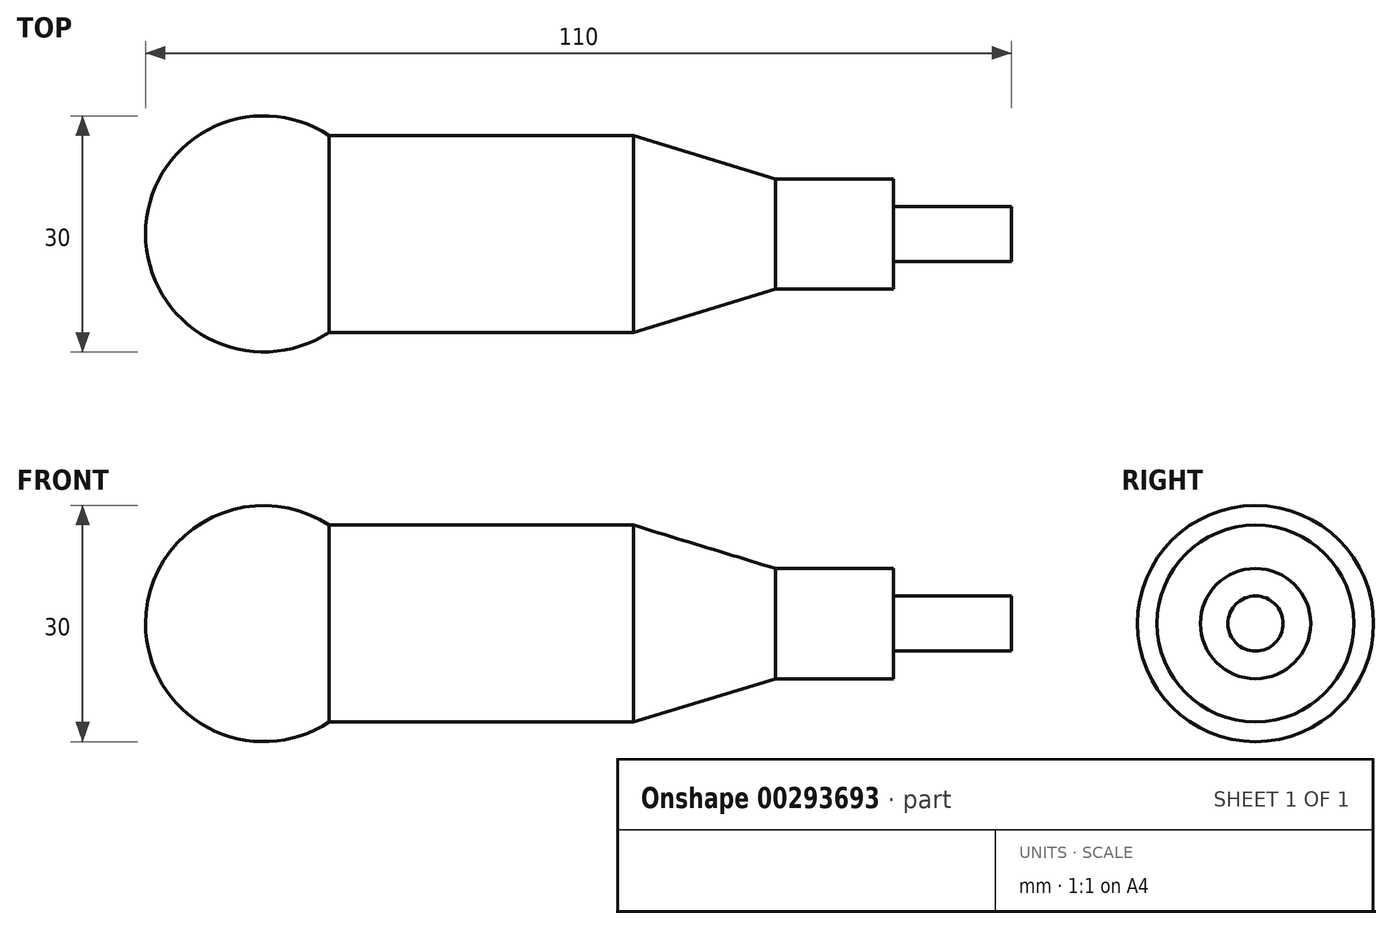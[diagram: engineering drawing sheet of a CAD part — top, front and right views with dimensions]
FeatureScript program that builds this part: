
annotation { "Feature Type Name" : "Feature", "Feature Type Description" : "" }
export const myFeature = defineFeature(function(context is Context, id is Id, definition is map)
    precondition{}
    {
        {
            var Q0;
            Q0=qCreatedBy(makeId("Front.planeOp"),FACE);
            var sketch = newSketch(context, id + "F0", { "sketchPlane" : qUnion([Q0])});
            skArc(sketch, "E0", {"start": v(8.3, 12.5) * mm, "mid": v(-7.1, 13.22) * mm, "end": v(-15, 0) * mm});
            skLineSegment(sketch, "E1", {"start": v(8.3, 12.5) * mm, "end": v(47, 12.5) * mm});
            skLineSegment(sketch, "E2", {"start": v(47, 12.5) * mm, "end": v(65, 7) * mm});
            skLineSegment(sketch, "E3", {"start": v(65, 7) * mm, "end": v(80, 7) * mm});
            skLineSegment(sketch, "E4", {"start": v(80, 7) * mm, "end": v(80, 3.5) * mm});
            skLineSegment(sketch, "E5", {"start": v(80, 3.5) * mm, "end": v(95, 3.5) * mm});
            skLineSegment(sketch, "E6", {"start": v(95, 3.5) * mm, "end": v(95, 0) * mm});
            skPoint(sketch, "E7.orphan", {"position": v(3.16, 12.5) * mm});
            skLineSegment(sketch, "E8", {"start": v(-15, 0) * mm, "end": v(95, 0) * mm});
            skSolve(sketch);
        }
        {
            var Q0;
            Q0=makeQuery(id+"F0.imprint","IMPRINT",FACE,{"disambiguationData":[TD([[makeQuery(id+"F0.imprint","IMPRINT",EDGE,{"derivedFrom":sQuery(id+"F0.wireOp",EDGE,"E0")}),1.0]])]});
            var Q1;
            Q1=sQuery(id+"F0.wireOp",EDGE,"E8");
            revolve(context, id + "F1", {"entities" : qUnion([Q0]), "axis" : qUnion([Q1]), "revolveType" : RevolveType.FULL});
        }
    });
